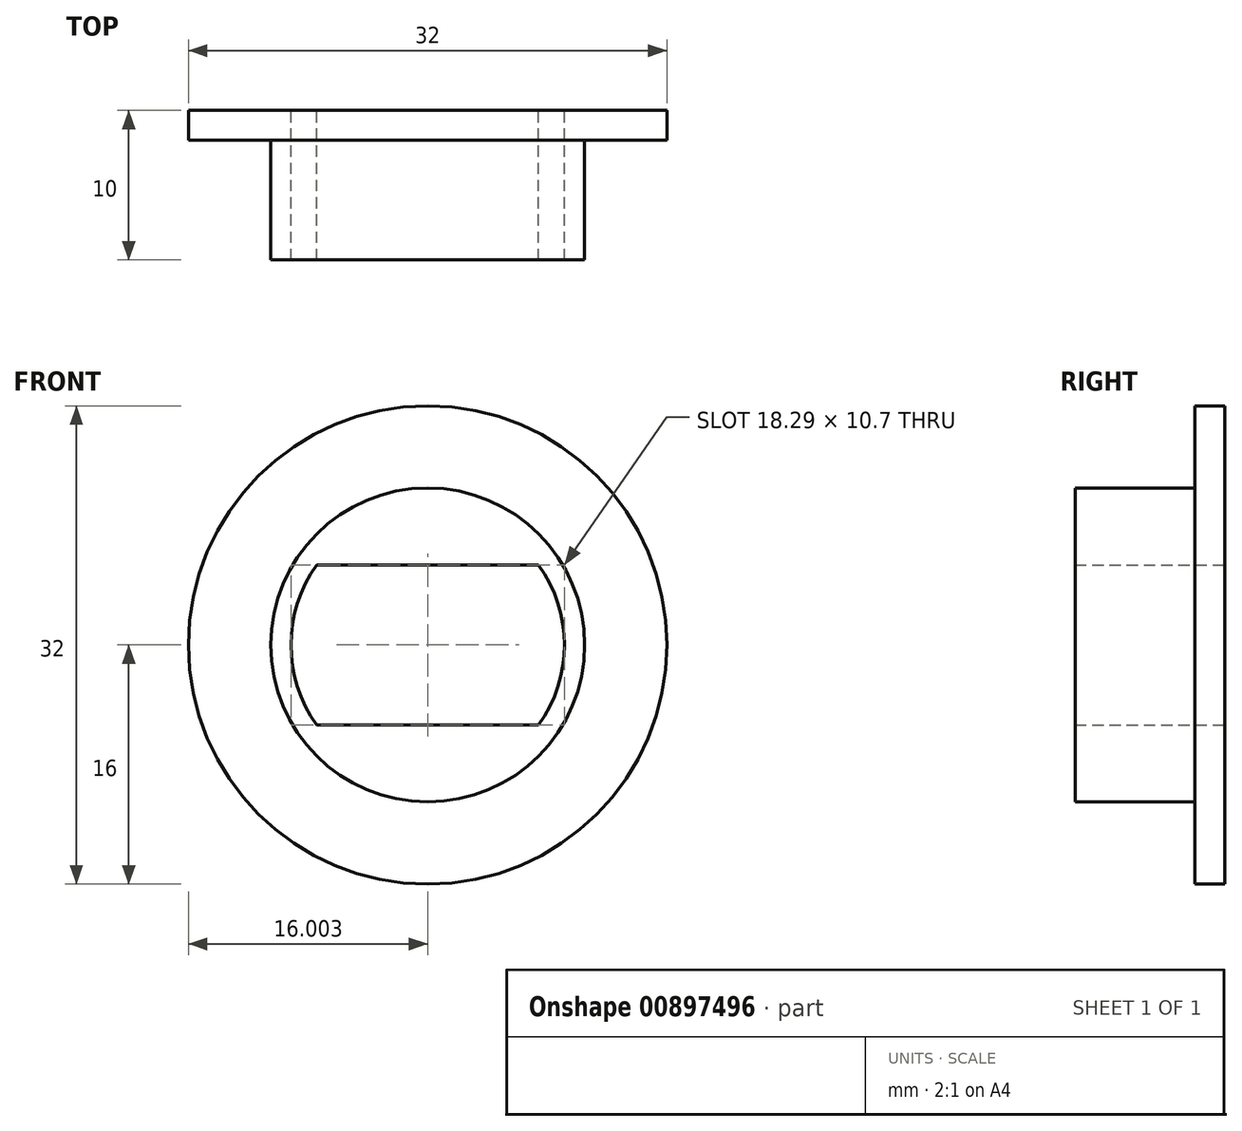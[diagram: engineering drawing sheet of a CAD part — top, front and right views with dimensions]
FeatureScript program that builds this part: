
annotation { "Feature Type Name" : "Feature", "Feature Type Description" : "" }
export const myFeature = defineFeature(function(context is Context, id is Id, definition is map)
    precondition{}
    {
        {
            var Q0;
            Q0=qCreatedBy(makeId("Front.planeOp"),FACE);
            var sketch = newSketch(context, id + "F0", { "sketchPlane" : qUnion([Q0])});
            skCircle(sketch, "E0", {"center": v(0, 0) * mm, "radius": 9.5 * mm});
            skCircle(sketch, "E1", {"center": v(0, 0) * mm, "radius": 16 * mm});
            skSolve(sketch);
        }
        {
            var Q0;
            Q0=makeQuery(id+"F0.imprint","IMPRINT",FACE,{"disambiguationData":[TD([[makeQuery(id+"F0.imprint","IMPRINT",EDGE,{"derivedFrom":sQuery(id+"F0.wireOp",EDGE,"E0")}),-1.0]])]});
            extrude(context, id + "F1", {"entities" : qUnion([Q0]), "depth" : 2 * mm, "offsetDistance" : 25.4 * mm});
        }
        {
            var Q0;
            Q0=qCreatedBy(makeId("Front.planeOp"),FACE);
            var sketch = newSketch(context, id + "F2", { "sketchPlane" : qUnion([Q0])});
            skLineSegment(sketch, "E2.MirrorCS", {"start": v(23.12, -5.4) * mm, "end": v(9.08, -5.28) * mm, "construction": true});
            skArc(sketch, "E3", {"start": v(9.1, 5.25) * mm, "mid": v(0, 10.5) * mm, "end": v(-9.1, 5.25) * mm});
            skLineSegment(sketch, "E4.trimOffspring", {"start": v(-9.1, -5.25) * mm, "end": v(-31.1, -5.25) * mm, "construction": true});
            skPoint(sketch, "E5.start.orphan", {"position": v(23.12, 5.4) * mm});
            skPoint(sketch, "E6.start.orphan", {"position": v(-7.41, 5.35) * mm});
            skArc(sketch, "E7.trimOffspring", {"start": v(-9.1, -5.25) * mm, "mid": v(-0.02, -10.5) * mm, "end": v(9.08, -5.28) * mm});
            skArc(sketch, "E8", {"start": v(9.1, 5.25) * mm, "mid": v(10.5, -0.02) * mm, "end": v(9.08, -5.28) * mm});
            skArc(sketch, "E9", {"start": v(-9.1, 5.25) * mm, "mid": v(-10.5, 0) * mm, "end": v(-9.1, -5.25) * mm});
            skPoint(sketch, "E10.trimOffspring.end.orphan", {"position": v(-31.1, 5.25) * mm});
            skArc(sketch, "E11", {"start": v(-7.41, 5.35) * mm, "mid": v(-9.14, 0) * mm, "end": v(-7.41, -5.35) * mm});
            skArc(sketch, "E12", {"start": v(7.42, 5.35) * mm, "mid": v(9.15, 0) * mm, "end": v(7.42, -5.35) * mm});
            skLineSegment(sketch, "E13", {"start": v(-7.41, -5.35) * mm, "end": v(7.42, -5.35) * mm});
            skLineSegment(sketch, "E14", {"start": v(-7.41, 5.35) * mm, "end": v(7.42, 5.35) * mm});
            skSolve(sketch);
        }
        {
            var Q0;
            Q0=makeQuery(id+"F2.imprint","IMPRINT",FACE,{"disambiguationData":[TD([[makeQuery(id+"F2.imprint","IMPRINT",EDGE,{"derivedFrom":sQuery(id+"F2.wireOp",EDGE,"E3")}),1.0]])]});
            extrude(context, id + "F3", {"entities" : qUnion([Q0]), "operationType" : NewBodyOperationType.ADD, "depth" : 10 * mm, "offsetDistance" : 25 * mm});
        }
    });
